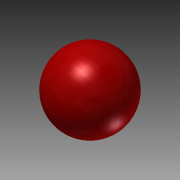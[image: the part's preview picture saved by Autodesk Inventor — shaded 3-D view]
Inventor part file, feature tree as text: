
AUTODESK INVENTOR PART (.ipt)
format: ipt  version: 2014 SP1 (Build 180222100, 222)  size: 135,680 bytes
history: native  units: in
note: dims shown in document units (in); Inventor stores cm internally (conversion verified against a paired STEP export)
features: revolve x1, sketch x1
ambient origin geometry x8: Origin, YZ Plane, XZ Plane, XY Plane, X Axis, Y Axis, Z Axis, Center Point
bodies: Solid1 (feature_tree)
feature tree (2):
  revolve  "Revolution1"  [1 undecoded]
  sketch  "Sketch1"  dims[d0=24.0in d1=0.125in d2=90.0deg]
note: 1 required parameter value undecoded (feature->parameter linkage not recoverable at this tier; creation-order binding heuristic only, values carry confidence <= 0.55)
